# Revit family: TCNH-B
name_source: partatom
category: Mechanical Equipment
units: mm (PartAtom-declared; Revit-internal decimal feet)

## family parameters
Always vertical = Yes
Cut with Voids When Loaded = No
Part Type = Normal
Room Calculation Point = No
Round Connector Dimension = Use Radius
Shared = No
Work Plane-Based = No

## types (20) — shared parameters
0 = 0' - 0"
1" = 0' - 1"
1.5 = 0' - 1 1/2"
1/4 = 0' - 0 1/4"
135 = 135.00°
2" = 0' - 2"
2' = 2' - 0"
4" = 0' - 4"
45 = 45.00°
Manufacturer = Loren Cook Company
Model = TCNH-B
ONE EIGTH = 0' - 0 1/8"
Type Comments = Tubular Centrifugal Inline Belt Drive Heavy Duty Arr. 9
URL = www.lorencook.com

## per-type parameters (varying)
- 60-TCNH-B: (A/4)+(A/12)=0' - 6 11/32"; (D+3)/2=0' - 10 3/4"; (D-3)/2=0' - 7 3/4"; (E+3)/2=0' - 8 27/32"; (E-3)/2=0' - 5 27/32"; (J+2")/2=0' - 11 15/32"; -(A/2)=-0' - 9 1/2"; -(C/2)=-0' - 11"; -C+1.5=-1' - 8 1/2"; A=1' - 7"; A/12=0' - 1 19/32"; A/2=0' - 9 1/2"; A/4=0' - 4 3/4"; B=1' - 4"; B-C=-0' - 6"; B/2=0' - 8"; B/3=0' - 5 11/32"; C=1' - 10"; C/2=0' - 11"; C/3*2=-0' - 7 11/32"; D=1' - 6 1/2"; D+3=1' - 9 1/2"; D-3=1' - 3 1/2"; D/2=0' - 9 1/4"; E=1' - 2 11/16"; E+3=1' - 5 11/16"; E-3=0' - 11 11/16"; E/2=0' - 7 11/32"; F=1' - 5 11/16"; G=0' - 10 1/8"; G+SQ=1' - 5 17/32"; G-SQ=0' - 2 23/32"; H=2' - 6 5/8"; H/2=1' - 3 5/16"; J=1' - 8 15/16"; J/2=0' - 10 15/32"; LONG=0' - 10 7/8"; SHORT=0' - 7 1/2"; SQRT((J^2)/2)=0' - 7 13/32"
- 70-TCNH-B: (A/4)+(A/12)=0' - 6 11/32"; (D+3)/2=0' - 10 3/4"; (D-3)/2=0' - 7 3/4"; (E+3)/2=0' - 8 27/32"; (E-3)/2=0' - 5 27/32"; (J+2")/2=0' - 11 15/32"; -(A/2)=-0' - 9 1/2"; -(C/2)=-0' - 11"; -C+1.5=-1' - 8 1/2"; A=1' - 7"; A/12=0' - 1 19/32"; A/2=0' - 9 1/2"; A/4=0' - 4 3/4"; B=1' - 4"; B-C=-0' - 6"; B/2=0' - 8"; B/3=0' - 5 11/32"; C=1' - 10"; C/2=0' - 11"; C/3*2=-0' - 7 11/32"; D=1' - 6 1/2"; D+3=1' - 9 1/2"; D-3=1' - 3 1/2"; D/2=0' - 9 1/4"; E=1' - 2 11/16"; E+3=1' - 5 11/16"; E-3=0' - 11 11/16"; E/2=0' - 7 11/32"; F=1' - 5 11/16"; G=0' - 10 1/8"; G+SQ=1' - 5 17/32"; G-SQ=0' - 2 23/32"; H=2' - 6 5/8"; H/2=1' - 3 5/16"; J=1' - 8 15/16"; J/2=0' - 10 15/32"; LONG=0' - 10 7/8"; SHORT=0' - 7 1/2"; SQRT((J^2)/2)=0' - 7 13/32"
- 80-TCNH-B: (A/4)+(A/12)=0' - 6 11/32"; (D+3)/2=0' - 10 3/4"; (D-3)/2=0' - 7 3/4"; (E+3)/2=0' - 8 27/32"; (E-3)/2=0' - 5 27/32"; (J+2")/2=0' - 11 15/32"; -(A/2)=-0' - 9 1/2"; -(C/2)=-0' - 11"; -C+1.5=-1' - 8 1/2"; A=1' - 7"; A/12=0' - 1 19/32"; A/2=0' - 9 1/2"; A/4=0' - 4 3/4"; B=1' - 4"; B-C=-0' - 6"; B/2=0' - 8"; B/3=0' - 5 11/32"; C=1' - 10"; C/2=0' - 11"; C/3*2=-0' - 7 11/32"; D=1' - 6 1/2"; D+3=1' - 9 1/2"; D-3=1' - 3 1/2"; D/2=0' - 9 1/4"; E=1' - 2 11/16"; E+3=1' - 5 11/16"; E-3=0' - 11 11/16"; E/2=0' - 7 11/32"; F=1' - 5 11/16"; G=0' - 10 1/8"; G+SQ=1' - 5 17/32"; G-SQ=0' - 2 23/32"; H=2' - 6 5/8"; H/2=1' - 3 5/16"; J=1' - 8 15/16"; J/2=0' - 10 15/32"; LONG=0' - 10 7/8"; SHORT=0' - 7 1/2"; SQRT((J^2)/2)=0' - 7 13/32"
- 100-TCNH-B: (A/4)+(A/12)=0' - 6 11/32"; (D+3)/2=0' - 10 3/4"; (D-3)/2=0' - 7 3/4"; (E+3)/2=0' - 8 27/32"; (E-3)/2=0' - 5 27/32"; (J+2")/2=0' - 11 15/32"; -(A/2)=-0' - 9 1/2"; -(C/2)=-0' - 11"; -C+1.5=-1' - 8 1/2"; A=1' - 7"; A/12=0' - 1 19/32"; A/2=0' - 9 1/2"; A/4=0' - 4 3/4"; B=1' - 4"; B-C=-0' - 6"; B/2=0' - 8"; B/3=0' - 5 11/32"; C=1' - 10"; C/2=0' - 11"; C/3*2=-0' - 7 11/32"; D=1' - 6 1/2"; D+3=1' - 9 1/2"; D-3=1' - 3 1/2"; D/2=0' - 9 1/4"; E=1' - 2 11/16"; E+3=1' - 5 11/16"; E-3=0' - 11 11/16"; E/2=0' - 7 11/32"; F=1' - 5 11/16"; G=0' - 10 1/8"; G+SQ=1' - 5 17/32"; G-SQ=0' - 2 23/32"; H=2' - 6 5/8"; H/2=1' - 3 5/16"; J=1' - 8 15/16"; J/2=0' - 10 15/32"; LONG=0' - 10 7/8"; SHORT=0' - 7 1/2"; SQRT((J^2)/2)=0' - 7 13/32"
- 120-TCNH-B: (A/4)+(A/12)=0' - 7"; (D+3)/2=0' - 11 1/4"; (D-3)/2=0' - 8 1/4"; (E+3)/2=0' - 9 9/16"; (E-3)/2=0' - 6 9/16"; (J+2")/2=1' - 0 15/32"; -(A/2)=-0' - 10 1/2"; -(C/2)=-0' - 11 1/2"; -C+1.5=-1' - 9 1/2"; A=1' - 9"; A/12=0' - 1 3/4"; A/2=0' - 10 1/2"; A/4=0' - 5 1/4"; B=1' - 6"; B-C=-0' - 5"; B/2=0' - 9"; B/3=0' - 6"; C=1' - 11"; C/2=0' - 11 1/2"; C/3*2=-0' - 7 21/32"; D=1' - 7 1/2"; D+3=1' - 10 1/2"; D-3=1' - 4 1/2"; D/2=0' - 9 3/4"; E=1' - 4 1/8"; E+3=1' - 7 1/8"; E-3=1' - 1 1/8"; E/2=0' - 8 1/16"; F=1' - 7 1/8"; G=0' - 10 7/8"; G+SQ=1' - 7"; G-SQ=0' - 2 3/4"; H=2' - 8 3/16"; H/2=1' - 4 3/32"; J=1' - 10 15/16"; J/2=0' - 11 15/32"; LONG=0' - 11 3/8"; SHORT=0' - 8"; SQRT((J^2)/2)=0' - 8 1/8"
- 490-TCNH-B: (A/4)+(A/12)=2' - 1 3/4"; (D+3)/2=3' - 4 13/32"; (D-3)/2=3' - 1 13/32"; (E+3)/2=2' - 7 13/16"; (E-3)/2=2' - 4 13/16"; (J+2")/2=3' - 7 7/8"; -(A/2)=-3' - 2 5/8"; -(C/2)=-3' - 0 1/4"; -C+1.5=-5' - 11"; A=6' - 5 1/4"; A/12=0' - 6 7/16"; A/2=3' - 2 5/8"; A/4=1' - 7 5/16"; B=6' - 1"; B-C=0' - 0 1/2"; B/2=3' - 0 1/2"; B/3=2' - 0 11/32"; C=6' - 0 1/2"; C/2=3' - 0 1/4"; C/3*2=-2' - 0 5/32"; D=6' - 5 13/16"; D+3=6' - 8 13/16"; D-3=6' - 2 13/16"; D/2=3' - 2 29/32"; E=5' - 0 5/8"; E+3=5' - 3 5/8"; E-3=4' - 9 5/8"; E/2=2' - 6 5/16"; F=5' - 9 7/16"; G=3' - 6 1/16"; G+SQ=6' - 0 3/8"; G-SQ=0' - 11 3/4"; H=8' - 10 1/4"; H/2=4' - 5 1/8"; J=7' - 1 3/4"; J/2=3' - 6 7/8"; LONG=3' - 5 9/16"; SHORT=3' - 0 1/8"; SQRT((J^2)/2)=2' - 6 5/16"
- 135-TCNH-B: (A/4)+(A/12)=0' - 8"; (D+3)/2=0' - 11 1/2"; (D-3)/2=0' - 8 1/2"; (E+3)/2=0' - 10 5/8"; (E-3)/2=0' - 7 5/8"; (J+2")/2=1' - 2"; -(A/2)=-1' - 0"; -(C/2)=-1' - 0 1/4"; -C+1.5=-1' - 11"; A=2' - 0"; A/12=0' - 2"; A/2=1' - 0"; A/4=0' - 6"; B=1' - 9"; B-C=-0' - 3 1/2"; B/2=0' - 10 1/2"; B/3=0' - 7"; C=2' - 0 1/2"; C/2=1' - 0 1/4"; C/3*2=-0' - 8 5/32"; D=1' - 8"; D+3=1' - 11"; D-3=1' - 5"; D/2=0' - 10"; E=1' - 6 1/4"; E+3=1' - 9 1/4"; E-3=1' - 3 1/4"; E/2=0' - 9 1/8"; F=1' - 9 1/4"; G=1' - 1 3/8"; G+SQ=1' - 10 9/16"; G-SQ=0' - 4 3/16"; H=3' - 0 3/4"; H/2=1' - 6 3/8"; J=2' - 2"; J/2=1' - 1"; LONG=1' - 0 1/8"; SHORT=0' - 7 3/4"; SQRT((J^2)/2)=0' - 9 3/16"
- 150-TCNH-B: (A/4)+(A/12)=0' - 9"; (D+3)/2=1' - 0 3/4"; (D-3)/2=0' - 9 3/4"; (E+3)/2=0' - 11 11/16"; (E-3)/2=0' - 8 11/16"; (J+2")/2=1' - 3 1/2"; -(A/2)=-1' - 1 1/2"; -(C/2)=-1' - 1 5/8"; -C+1.5=-2' - 1 3/4"; A=2' - 3"; A/12=0' - 2 1/4"; A/2=1' - 1 1/2"; A/4=0' - 6 3/4"; B=2' - 0"; B-C=-0' - 3 1/4"; B/2=1' - 0"; B/3=0' - 8"; C=2' - 3 1/4"; C/2=1' - 1 5/8"; C/3*2=-0' - 9 3/32"; D=1' - 10 1/2"; D+3=2' - 1 1/2"; D-3=1' - 7 1/2"; D/2=0' - 11 1/4"; E=1' - 8 3/8"; E+3=1' - 11 3/8"; E-3=1' - 5 3/8"; E/2=0' - 10 3/16"; F=1' - 11 3/8"; G=1' - 2 1/2"; G+SQ=2' - 0 3/4"; G-SQ=0' - 4 1/4"; H=3' - 7 1/4"; H/2=1' - 9 5/8"; J=2' - 5"; J/2=1' - 2 1/2"; LONG=1' - 1 1/2"; SHORT=0' - 8 7/8"; SQRT((J^2)/2)=0' - 10 1/4"
- 165-TCNH-B: (A/4)+(A/12)=0' - 9 21/32"; (D+3)/2=1' - 1"; (D-3)/2=0' - 10"; (E+3)/2=1' - 0 7/8"; (E-3)/2=0' - 9 7/8"; (J+2")/2=1' - 5 3/16"; -(A/2)=-1' - 2 1/2"; -(C/2)=-1' - 2 3/8"; -C+1.5=-2' - 3 1/4"; A=2' - 5"; A/12=0' - 2 13/32"; A/2=1' - 2 1/2"; A/4=0' - 7 1/4"; B=2' - 2"; B-C=-0' - 2 3/4"; B/2=1' - 1"; B/3=0' - 8 21/32"; C=2' - 4 3/4"; C/2=1' - 2 3/8"; C/3*2=-0' - 9 19/32"; D=1' - 11"; D+3=2' - 2"; D-3=1' - 8"; D/2=0' - 11 1/2"; E=1' - 10 3/4"; E+3=2' - 1 3/4"; E-3=1' - 7 3/4"; E/2=0' - 11 3/8"; F=2' - 2 7/8"; G=1' - 3 3/4"; G+SQ=2' - 3 3/16"; G-SQ=0' - 4 5/16"; H=3' - 9 3/4"; H/2=1' - 10 7/8"; J=2' - 8 3/8"; J/2=1' - 4 3/16"; LONG=1' - 2 1/4"; SHORT=0' - 8 5/8"; SQRT((J^2)/2)=0' - 11 7/16"
- 180-TCNH-B: (A/4)+(A/12)=0' - 10 11/32"; (D+3)/2=1' - 2 3/4"; (D-3)/2=0' - 11 3/4"; (E+3)/2=1' - 1 29/32"; (E-3)/2=0' - 10 29/32"; (J+2")/2=1' - 6 7/32"; -(A/2)=-1' - 3 1/2"; -(C/2)=-1' - 3 5/8"; -C+1.5=-2' - 5 3/4"; A=2' - 7"; A/12=0' - 2 19/32"; A/2=1' - 3 1/2"; A/4=0' - 7 3/4"; B=2' - 4"; B-C=-0' - 3 1/4"; B/2=1' - 2"; B/3=0' - 9 11/32"; C=2' - 7 1/4"; C/2=1' - 3 5/8"; C/3*2=-0' - 10 13/32"; D=2' - 2 1/2"; D+3=2' - 5 1/2"; D-3=1' - 11 1/2"; D/2=1' - 1 1/4"; E=2' - 0 13/16"; E+3=2' - 3 13/16"; E-3=1' - 9 13/16"; E/2=1' - 0 13/32"; F=2' - 4 3/16"; G=1' - 4 3/8"; G+SQ=2' - 4 9/16"; G-SQ=0' - 4 3/16"; H=3' - 11 3/4"; H/2=1' - 11 7/8"; J=2' - 10 7/16"; J/2=1' - 5 7/32"; LONG=1' - 3 1/2"; SHORT=0' - 10 7/8"; SQRT((J^2)/2)=1' - 0 3/16"
- 195-TCNH-B: (A/4)+(A/12)=0' - 11 11/32"; (D+3)/2=1' - 3 3/8"; (D-3)/2=1' - 0 3/8"; (E+3)/2=1' - 3 3/8"; (E-3)/2=1' - 0 3/8"; (J+2")/2=1' - 8 23/32"; -(A/2)=-1' - 5"; -(C/2)=-1' - 4 3/4"; -C+1.5=-2' - 8"; A=2' - 10"; A/12=0' - 2 27/32"; A/2=1' - 5"; A/4=0' - 8 1/2"; B=2' - 7"; B-C=-0' - 2 1/2"; B/2=1' - 3 1/2"; B/3=0' - 10 11/32"; C=2' - 9 1/2"; C/2=1' - 4 3/4"; C/3*2=-0' - 11 5/32"; D=2' - 3 3/4"; D+3=2' - 6 3/4"; D-3=2' - 0 3/4"; D/2=1' - 1 7/8"; E=2' - 3 3/4"; E+3=2' - 6 3/4"; E-3=2' - 0 3/4"; E/2=1' - 1 7/8"; F=2' - 8 3/4"; G=1' - 7 1/8"; G+SQ=2' - 9 1/16"; G-SQ=0' - 5 3/16"; H=4' - 4 3/16"; H/2=2' - 2 3/32"; J=3' - 3 7/16"; J/2=1' - 7 23/32"; LONG=1' - 4 5/8"; SHORT=0' - 11"; SQRT((J^2)/2)=1' - 1 15/16"
- 210-TCNH-B: (A/4)+(A/12)=1' - 0 11/32"; (D+3)/2=1' - 4"; (D-3)/2=1' - 1"; (E+3)/2=1' - 4 7/16"; (E-3)/2=1' - 1 7/16"; (J+2")/2=1' - 10 7/32"; -(A/2)=-1' - 6 1/2"; -(C/2)=-1' - 5 3/8"; -C+1.5=-2' - 9 1/4"; A=3' - 1"; A/12=0' - 3 3/32"; A/2=1' - 6 1/2"; A/4=0' - 9 1/4"; B=2' - 10"; B-C=-0' - 0 3/4"; B/2=1' - 5"; B/3=0' - 11 11/32"; C=2' - 10 3/4"; C/2=1' - 5 3/8"; C/3*2=-0' - 11 19/32"; D=2' - 5"; D+3=2' - 8"; D-3=2' - 2"; D/2=1' - 2 1/2"; E=2' - 5 7/8"; E+3=2' - 8 7/8"; E-3=2' - 2 7/8"; E/2=1' - 2 15/16"; F=3' - 1 7/8"; G=1' - 8 3/16"; G+SQ=2' - 11 3/16"; G-SQ=0' - 5 3/16"; H=4' - 7 1/8"; H/2=2' - 3 9/16"; J=3' - 6 7/16"; J/2=1' - 9 7/32"; LONG=1' - 5 1/4"; SHORT=0' - 11 5/8"; SQRT((J^2)/2)=1' - 3"
- 225-TCNH-B: (A/4)+(A/12)=1' - 1 13/32"; (D+3)/2=1' - 9 15/16"; (D-3)/2=1' - 6 15/16"; (E+3)/2=1' - 6 5/8"; (E-3)/2=1' - 3 5/8"; (J+2")/2=2' - 1 7/32"; -(A/2)=-1' - 8 1/8"; -(C/2)=-1' - 5 3/4"; -C+1.5=-2' - 10"; A=3' - 4 1/4"; A/12=0' - 3 11/32"; A/2=1' - 8 1/8"; A/4=0' - 10 1/16"; B=3' - 0"; B-C=0' - 0 1/2"; B/2=1' - 6"; B/3=1' - 0"; C=2' - 11 1/2"; C/2=1' - 5 3/4"; C/3*2=-0' - 11 27/32"; D=3' - 4 7/8"; D+3=3' - 7 7/8"; D-3=3' - 1 7/8"; D/2=1' - 8 7/16"; E=2' - 10 1/4"; E+3=3' - 1 1/4"; E-3=2' - 7 1/4"; E/2=1' - 5 1/8"; F=3' - 6 1/16"; G=1' - 10 7/8"; G+SQ=3' - 4"; G-SQ=0' - 5 3/4"; H=5' - 2 1/8"; H/2=2' - 7 1/16"; J=4' - 0 7/16"; J/2=2' - 0 7/32"; LONG=1' - 11 1/8"; SHORT=1' - 5 5/8"; SQRT((J^2)/2)=1' - 5 1/8"
- 245-TCNH-B: (A/4)+(A/12)=1' - 2 3/4"; (D+3)/2=2' - 0 11/16"; (D-3)/2=1' - 9 11/16"; (E+3)/2=1' - 8 1/16"; (E-3)/2=1' - 5 1/16"; (J+2")/2=2' - 3 1/4"; -(A/2)=-1' - 10 1/8"; -(C/2)=-1' - 8 1/2"; -C+1.5=-3' - 3 1/2"; A=3' - 8 1/4"; A/12=0' - 3 11/16"; A/2=1' - 10 1/8"; A/4=0' - 11 1/16"; B=3' - 4"; B-C=-0' - 1"; B/2=1' - 8"; B/3=1' - 1 11/32"; C=3' - 5"; C/2=1' - 8 1/2"; C/3*2=-1' - 1 21/32"; D=3' - 10 3/8"; D+3=4' - 1 3/8"; D-3=3' - 7 3/8"; D/2=1' - 11 3/16"; E=3' - 1 1/8"; E+3=3' - 4 1/8"; E-3=2' - 10 1/8"; E/2=1' - 6 9/16"; F=3' - 8 15/16"; G=2' - 0 5/16"; G+SQ=3' - 6 7/8"; G-SQ=0' - 5 3/4"; H=5' - 5 7/8"; H/2=2' - 8 15/16"; J=4' - 4 1/2"; J/2=2' - 2 1/4"; LONG=2' - 1 7/8"; SHORT=1' - 8 3/8"; SQRT((J^2)/2)=1' - 6 9/16"
- 270-TCNH-B: (A/4)+(A/12)=1' - 4 3/32"; (D+3)/2=2' - 3 13/32"; (D-3)/2=2' - 0 13/32"; (E+3)/2=1' - 9 1/2"; (E-3)/2=1' - 6 1/2"; (J+2")/2=2' - 5 9/32"; -(A/2)=-2' - 0 1/8"; -(C/2)=-1' - 11 1/4"; -C+1.5=-3' - 9"; A=4' - 0 1/4"; A/12=0' - 4 1/32"; A/2=2' - 0 1/8"; A/4=1' - 0 1/16"; B=3' - 8"; B-C=-0' - 2 1/2"; B/2=1' - 10"; B/3=1' - 2 21/32"; C=3' - 10 1/2"; C/2=1' - 11 1/4"; C/3*2=-1' - 3 1/2"; D=4' - 3 13/16"; D+3=4' - 6 13/16"; D-3=4' - 0 13/16"; D/2=2' - 1 29/32"; E=3' - 4"; E+3=3' - 7"; E-3=3' - 1"; E/2=1' - 8"; F=3' - 11 3/4"; G=2' - 1 3/4"; G+SQ=3' - 9 3/4"; G-SQ=0' - 5 3/4"; H=5' - 11 5/8"; H/2=2' - 11 13/16"; J=4' - 8 9/16"; J/2=2' - 4 9/32"; LONG=2' - 4 9/16"; SHORT=1' - 11 1/8"; SQRT((J^2)/2)=1' - 8"
- 300-TCNH-B: (A/4)+(A/12)=1' - 5 13/32"; (D+3)/2=2' - 4 9/32"; (D-3)/2=2' - 1 9/32"; (E+3)/2=1' - 10 15/16"; (E-3)/2=1' - 7 15/16"; (J+2")/2=2' - 7 9/32"; -(A/2)=-2' - 2 1/8"; -(C/2)=-2' - 0 1/8"; -C+1.5=-3' - 10 3/4"; A=4' - 4 1/4"; A/12=0' - 4 11/32"; A/2=2' - 2 1/8"; A/4=1' - 1 1/16"; B=4' - 0"; B-C=-0' - 0 1/4"; B/2=2' - 0"; B/3=1' - 4"; C=4' - 0 1/4"; C/2=2' - 0 1/8"; C/3*2=-1' - 4 3/32"; D=4' - 5 9/16"; D+3=4' - 8 9/16"; D-3=4' - 2 9/16"; D/2=2' - 2 25/32"; E=3' - 6 7/8"; E+3=3' - 9 7/8"; E-3=3' - 3 7/8"; E/2=1' - 9 7/16"; F=4' - 2 5/8"; G=2' - 5 3/16"; G+SQ=4' - 2 19/32"; G-SQ=0' - 7 25/32"; H=6' - 3 7/8"; H/2=3' - 1 15/16"; J=5' - 0 9/16"; J/2=2' - 6 9/32"; LONG=2' - 5 7/16"; SHORT=2' - 0"; SQRT((J^2)/2)=1' - 9 13/32"
- 330-TCNH-B: (A/4)+(A/12)=1' - 6 3/4"; (D+3)/2=2' - 6 3/32"; (D-3)/2=2' - 3 3/32"; (E+3)/2=2' - 0 3/8"; (E-3)/2=1' - 9 3/8"; (J+2")/2=2' - 9 5/16"; -(A/2)=-2' - 4 1/8"; -(C/2)=-2' - 2"; -C+1.5=-4' - 2 1/2"; A=4' - 8 1/4"; A/12=0' - 4 11/16"; A/2=2' - 4 1/8"; A/4=1' - 2 1/16"; B=4' - 4"; B-C=0' - 0"; B/2=2' - 2"; B/3=1' - 5 11/32"; C=4' - 4"; C/2=2' - 2"; C/3*2=-1' - 5 11/32"; D=4' - 9 3/16"; D+3=5' - 0 3/16"; D-3=4' - 6 3/16"; D/2=2' - 4 19/32"; E=3' - 9 3/4"; E+3=4' - 0 3/4"; E-3=3' - 6 3/4"; E/2=1' - 10 7/8"; F=4' - 5 1/2"; G=2' - 6 9/16"; G+SQ=4' - 5 13/32"; G-SQ=0' - 7 23/32"; H=6' - 8 1/2"; H/2=3' - 4 1/4"; J=5' - 4 5/8"; J/2=2' - 8 5/16"; LONG=2' - 7 3/16"; SHORT=2' - 1 7/8"; SQRT((J^2)/2)=1' - 10 27/32"
- 365-TCNH-B: (A/4)+(A/12)=1' - 7 13/32"; (D+3)/2=2' - 7 3/32"; (D-3)/2=2' - 4 3/32"; (E+3)/2=2' - 1 1/16"; (E-3)/2=1' - 10 1/16"; (J+2")/2=2' - 10 5/16"; -(A/2)=-2' - 5 1/8"; -(C/2)=-2' - 3"; -C+1.5=-4' - 4 1/2"; A=4' - 10 1/4"; A/12=0' - 4 27/32"; A/2=2' - 5 1/8"; A/4=1' - 2 9/16"; B=4' - 6"; B-C=0' - 0"; B/2=2' - 3"; B/3=1' - 6"; C=4' - 6"; C/2=2' - 3"; C/3*2=-1' - 6"; D=4' - 11 3/16"; D+3=5' - 2 3/16"; D-3=4' - 8 3/16"; D/2=2' - 5 19/32"; E=3' - 11 1/8"; E+3=4' - 2 1/8"; E-3=3' - 8 1/8"; E/2=1' - 11 9/16"; F=4' - 6 15/16"; G=2' - 9 5/16"; G+SQ=4' - 8 7/8"; G-SQ=0' - 9 3/4"; H=6' - 11 5/16"; H/2=3' - 5 21/32"; J=5' - 6 5/8"; J/2=2' - 9 5/16"; LONG=2' - 8 3/16"; SHORT=2' - 2 7/8"; SQRT((J^2)/2)=1' - 11 9/16"
- 445-TCNH-B: (A/4)+(A/12)=1' - 11 13/32"; (D+3)/2=3' - 1 5/32"; (D-3)/2=2' - 10 5/32"; (E+3)/2=2' - 5 11/32"; (E-3)/2=2' - 2 11/32"; (J+2")/2=3' - 4 5/16"; -(A/2)=-2' - 11 1/8"; -(C/2)=-2' - 9"; -C+1.5=-5' - 4 1/2"; A=5' - 10 1/4"; A/12=0' - 5 27/32"; A/2=2' - 11 1/8"; A/4=1' - 5 9/16"; B=5' - 6"; B-C=0' - 0"; B/2=2' - 9"; B/3=1' - 10"; C=5' - 6"; C/2=2' - 9"; C/3*2=-1' - 10"; D=5' - 11 5/16"; D+3=6' - 2 5/16"; D-3=5' - 8 5/16"; D/2=2' - 11 21/32"; E=4' - 7 11/16"; E+3=4' - 10 11/16"; E-3=4' - 4 11/16"; E/2=2' - 3 27/32"; F=5' - 3 7/16"; G=3' - 3 9/16"; G+SQ=5' - 7 3/8"; G-SQ=0' - 11 3/4"; H=8' - 3 1/16"; H/2=4' - 1 17/32"; J=6' - 6 5/8"; J/2=3' - 3 5/16"; LONG=3' - 2 5/16"; SHORT=2' - 8 7/8"; SQRT((J^2)/2)=2' - 3 13/16"
- 402-TCNH-B: (A/4)+(A/12)=1' - 9 13/32"; (D+3)/2=2' - 9 29/32"; (D-3)/2=2' - 6 29/32"; (E+3)/2=2' - 3 3/16"; (E-3)/2=2' - 0 3/16"; (J+2")/2=3' - 1 5/16"; -(A/2)=-2' - 8 1/8"; -(C/2)=-2' - 5 3/4"; -C+1.5=-4' - 10"; A=5' - 4 1/4"; A/12=0' - 5 11/32"; A/2=2' - 8 1/8"; A/4=1' - 4 1/16"; B=5' - 0"; B-C=0' - 0 1/2"; B/2=2' - 6"; B/3=1' - 8"; C=4' - 11 1/2"; C/2=2' - 5 3/4"; C/3*2=-1' - 7 27/32"; D=5' - 4 13/16"; D+3=5' - 7 13/16"; D-3=5' - 1 13/16"; D/2=2' - 8 13/32"; E=4' - 3 3/8"; E+3=4' - 6 3/8"; E-3=4' - 0 3/8"; E/2=2' - 1 11/16"; F=4' - 11 3/16"; G=2' - 11 7/16"; G+SQ=5' - 1 1/8"; G-SQ=0' - 9 3/4"; H=7' - 8 5/8"; H/2=3' - 10 5/16"; J=6' - 0 5/8"; J/2=3' - 0 5/16"; LONG=2' - 11 1/16"; SHORT=2' - 5 5/8"; SQRT((J^2)/2)=2' - 1 11/16"

## geometry (parser evidence)
native form markers: Sweep x1
no freeform markers — native parametric forms only
